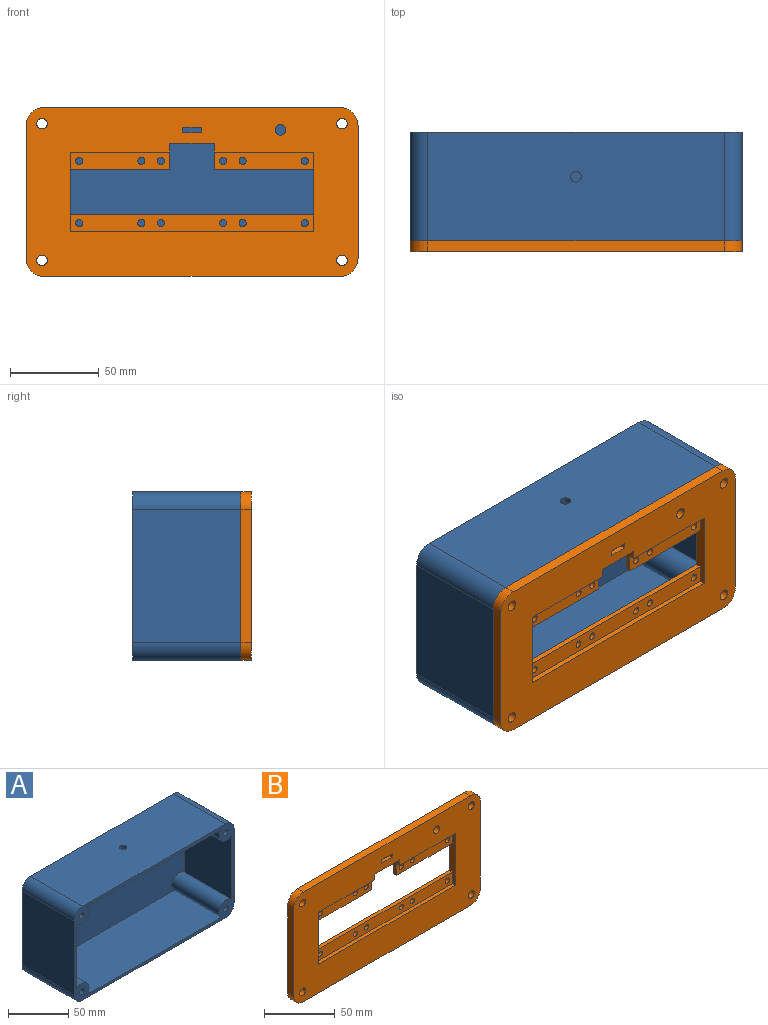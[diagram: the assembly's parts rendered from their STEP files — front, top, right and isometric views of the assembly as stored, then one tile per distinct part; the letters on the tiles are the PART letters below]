
ASSEMBLY  parts=2 mates=1
PART A: 32 faces, bbox 187x61x95 mm
  f0: cylinder r=3mm len=51mm, axis (0,1,0), area 961.3mm2, adj f17,f28
  f1: cylinder r=3mm len=51mm, axis (0,1,0), area 961.3mm2, adj f17,f26
  f2: cylinder r=3mm len=51mm, axis (0,1,0), area 961.3mm2, adj f17,f24
  f3: cylinder r=3mm len=51mm, axis (0,1,0), area 961.3mm2, adj f17,f30
  f4: plane 75x61mm, normal (1,0,0), area 4575mm2, adj f8,f17,f19,f22
  f5: plane 167x61mm, normal (0,0,1), area 10158.7mm2, adj f8,f17,f19,f20,f31
  f6: plane 75x61mm, normal (-1,0,0), area 4575mm2, adj f8,f17,f20,f21
  f7: plane 167x61mm, normal (0,0,-1), area 10187mm2, adj f8,f17,f21,f22
  f8: plane 187x95mm, normal (0,1,0), area 17299mm2, adj f4,f5,f6,f7,f19,f20,f21,f22
  f9: plane 64.98x55mm, normal (-1,0,0), area 3573.9mm2, adj f10,f16,f17,f18
  f10: cylinder r=8.5mm len=55mm, axis (0,1,0), area 1493mm2, adj f9,f11,f17,f18
  f11: plane 156.96x55mm, normal (0,0,1), area 8632.9mm2, adj f10,f12,f17,f18
  f12: cylinder r=8.5mm len=55mm, axis (0,1,0), area 1451.1mm2, adj f11,f13,f17,f18
  f13: plane 64.96x55mm, normal (1,0,0), area 3572.7mm2, adj f12,f14,f17,f18
  f14: cylinder r=8.5mm len=55mm, axis (0,1,0), area 1410.2mm2, adj f13,f15,f17,f18
  f15: plane 157.01x55mm, normal (0,0,-1), area 8607mm2, adj f14,f16,f17,f18,f31
  f16: cylinder r=8.5mm len=55mm, axis (0,1,0), area 1437mm2, adj f9,f15,f17,f18
  f17: plane 187x95mm, normal (0,-1,0), area 2186.7mm2, adj f0,f1,f2,f3,f4,f5,f6,f7
  f18: plane 181x89mm, normal (0,-1,0), area 15379.4mm2, adj f9,f10,f11,f12,f13,f14,f15,f16
  f19: cylinder r=10mm len=61mm, axis (0,-1,0), area 958.2mm2, adj f4,f5,f8,f17
  f20: cylinder r=10mm len=61mm, axis (0,1,0), area 958.2mm2, adj f5,f6,f8,f17
  f21: cylinder r=10mm len=61mm, axis (0,-1,0), area 958.2mm2, adj f6,f7,f8,f17
  f22: cylinder r=10mm len=61mm, axis (0,1,0), area 958.2mm2, adj f4,f7,f8,f17
  f23: cylinder r=5.5mm len=11mm, axis (0,1,0), area 345.6mm2, adj f8,f24
  f24: plane 11x11mm, normal (0,1,0), area 66.8mm2, adj f2,f23
  f25: cylinder r=5.5mm len=11mm, axis (0,1,0), area 345.6mm2, adj f8,f26
  f26: plane 11x11mm, normal (0,1,0), area 66.8mm2, adj f1,f25
  f27: cylinder r=5.5mm len=11mm, axis (0,1,0), area 345.6mm2, adj f8,f28
  f28: plane 11x11mm, normal (0,1,0), area 66.8mm2, adj f0,f27
  f29: cylinder r=5.5mm len=11mm, axis (0,1,0), area 345.6mm2, adj f8,f30
  f30: plane 11x11mm, normal (0,1,0), area 66.8mm2, adj f3,f29
  f31: cylinder r=3mm len=6mm, axis (0,0,1), area 56.5mm2, adj f5,f15
PART B: 50 faces, bbox 187x6x95 mm
  f0: plane 137x3mm, normal (0,0,1), area 411mm2, adj f1,f4,f22,f42
  f1: plane 45x6mm, normal (1,0,0), area 210mm2, adj f0,f2,f9,f22,f37,f41,f42,f43
  f2: plane 56x3mm, normal (0,0,-1), area 168mm2, adj f1,f10,f22,f41
  f3: plane 56x3mm, normal (0,0,-1), area 168mm2, adj f4,f12,f22,f36
  f4: plane 45x6mm, normal (-1,0,0), area 210mm2, adj f0,f3,f9,f22,f32,f36,f42,f43
  f5: plane 10.25x3mm, normal (0,0,-1), area 30.8mm2, adj f6,f8,f22,f31
  f6: plane 3x3mm, normal (-1,0,0), area 9mm2, adj f5,f7,f22,f31
  f7: plane 10.25x3mm, normal (0,0,1), area 30.8mm2, adj f6,f8,f22,f31
  f8: plane 3x3mm, normal (1,0,0), area 9mm2, adj f5,f7,f22,f31
  f9: plane 187x95mm, normal (0,1,0), area 13467mm2, adj f1,f4,f10,f11,f12,f13,f14,f15
  f10: plane 15x6mm, normal (1,0,0), area 60mm2, adj f2,f9,f11,f22,f37,f41
  f11: plane 25x6mm, normal (0,0,-1), area 150mm2, adj f9,f10,f12,f22
  f12: plane 15x6mm, normal (-1,0,0), area 60mm2, adj f3,f9,f11,f22,f32,f36
  f13: plane 75x6mm, normal (1,0,0), area 450mm2, adj f9,f22,f23,f26
  f14: plane 167x6mm, normal (0,0,1), area 1002mm2, adj f9,f22,f23,f24
  f15: plane 75x6mm, normal (-1,0,0), area 450mm2, adj f9,f22,f24,f25
  f16: cylinder r=3mm len=6mm, axis (0,1,0), area 113.1mm2, adj f9,f22
  f17: cylinder r=3mm len=6mm, axis (0,1,0), area 113.1mm2, adj f9,f22
  f18: cylinder r=3mm len=6mm, axis (0,1,0), area 113.1mm2, adj f9,f22
  f19: cylinder r=3mm len=6mm, axis (0,1,0), area 113.1mm2, adj f9,f22
  f20: cylinder r=3mm len=6mm, axis (0,1,0), area 113.1mm2, adj f9,f22
  f21: plane 167x6mm, normal (0,0,-1), area 1002mm2, adj f9,f22,f25,f26
  f22: plane 187x95mm, normal (0,-1,0), area 11217mm2, adj f0,f1,f2,f3,f4,f5,f6,f7
  f23: cylinder r=10mm len=10mm, axis (0,-1,0), area 94.2mm2, adj f9,f13,f14,f22
  f24: cylinder r=10mm len=10mm, axis (0,1,0), area 94.2mm2, adj f9,f14,f15,f22
  f25: cylinder r=10mm len=10mm, axis (0,-1,0), area 94.2mm2, adj f9,f15,f21,f22
  f26: cylinder r=10mm len=10mm, axis (0,1,0), area 94.2mm2, adj f9,f13,f21,f22
  f27: plane 8x3mm, normal (1,0,0), area 24mm2, adj f9,f28,f30,f31
  f28: plane 15x3mm, normal (0,0,-1), area 45mm2, adj f9,f27,f29,f31
  f29: plane 8x3mm, normal (-1,0,0), area 24mm2, adj f9,f28,f30,f31
  f30: plane 15x3mm, normal (0,0,1), area 45mm2, adj f9,f27,f29,f31
  f31: plane 15x8mm, normal (0,1,0), area 89.3mm2, adj f5,f6,f7,f8,f27,f28,f29,f30
  f32: plane 56x3mm, normal (0,0,-1), area 168mm2, adj f4,f9,f12,f36
  f33: cylinder r=2mm len=4mm, axis (0,1,0), area 37.7mm2, adj f9,f36
  f34: cylinder r=2mm len=4mm, axis (0,1,0), area 37.7mm2, adj f9,f36
  f35: cylinder r=2mm len=4mm, axis (0,1,0), area 37.7mm2, adj f9,f36
  f36: plane 56x10mm, normal (0,-1,0), area 522.3mm2, adj f3,f4,f12,f32,f33,f34,f35
  f37: plane 56x3mm, normal (0,0,-1), area 168mm2, adj f1,f9,f10,f41
  f38: cylinder r=2mm len=4mm, axis (0,1,0), area 37.7mm2, adj f9,f41
  f39: cylinder r=2mm len=4mm, axis (0,1,0), area 37.7mm2, adj f9,f41
  f40: cylinder r=2mm len=4mm, axis (0,1,0), area 37.7mm2, adj f9,f41
  f41: plane 56x10mm, normal (0,-1,0), area 522.3mm2, adj f1,f2,f10,f37,f38,f39,f40
  f42: plane 137x10mm, normal (0,-1,0), area 1294.6mm2, adj f0,f1,f4,f43,f44,f45,f46,f47
  f43: plane 137x3mm, normal (0,0,1), area 411mm2, adj f1,f4,f9,f42
  f44: cylinder r=2mm len=4mm, axis (0,1,0), area 37.7mm2, adj f9,f42
  f45: cylinder r=2mm len=4mm, axis (0,1,0), area 37.7mm2, adj f9,f42
  f46: cylinder r=2mm len=4mm, axis (0,1,0), area 37.7mm2, adj f9,f42
  f47: cylinder r=2mm len=4mm, axis (0,1,0), area 37.7mm2, adj f9,f42
  f48: cylinder r=2mm len=4mm, axis (0,1,0), area 37.7mm2, adj f9,f42
  f49: cylinder r=2mm len=4mm, axis (0,1,0), area 37.7mm2, adj f9,f42
PLACE A t=(-77.38,-1.88,-31.81)mm
PLACE B t=(-77.38,-62.88,-31.81)mm
MATE fastened A.f2 <-> B.f20  axis (0,-1,0) through (-161.88,-62.88,6.69)mm
